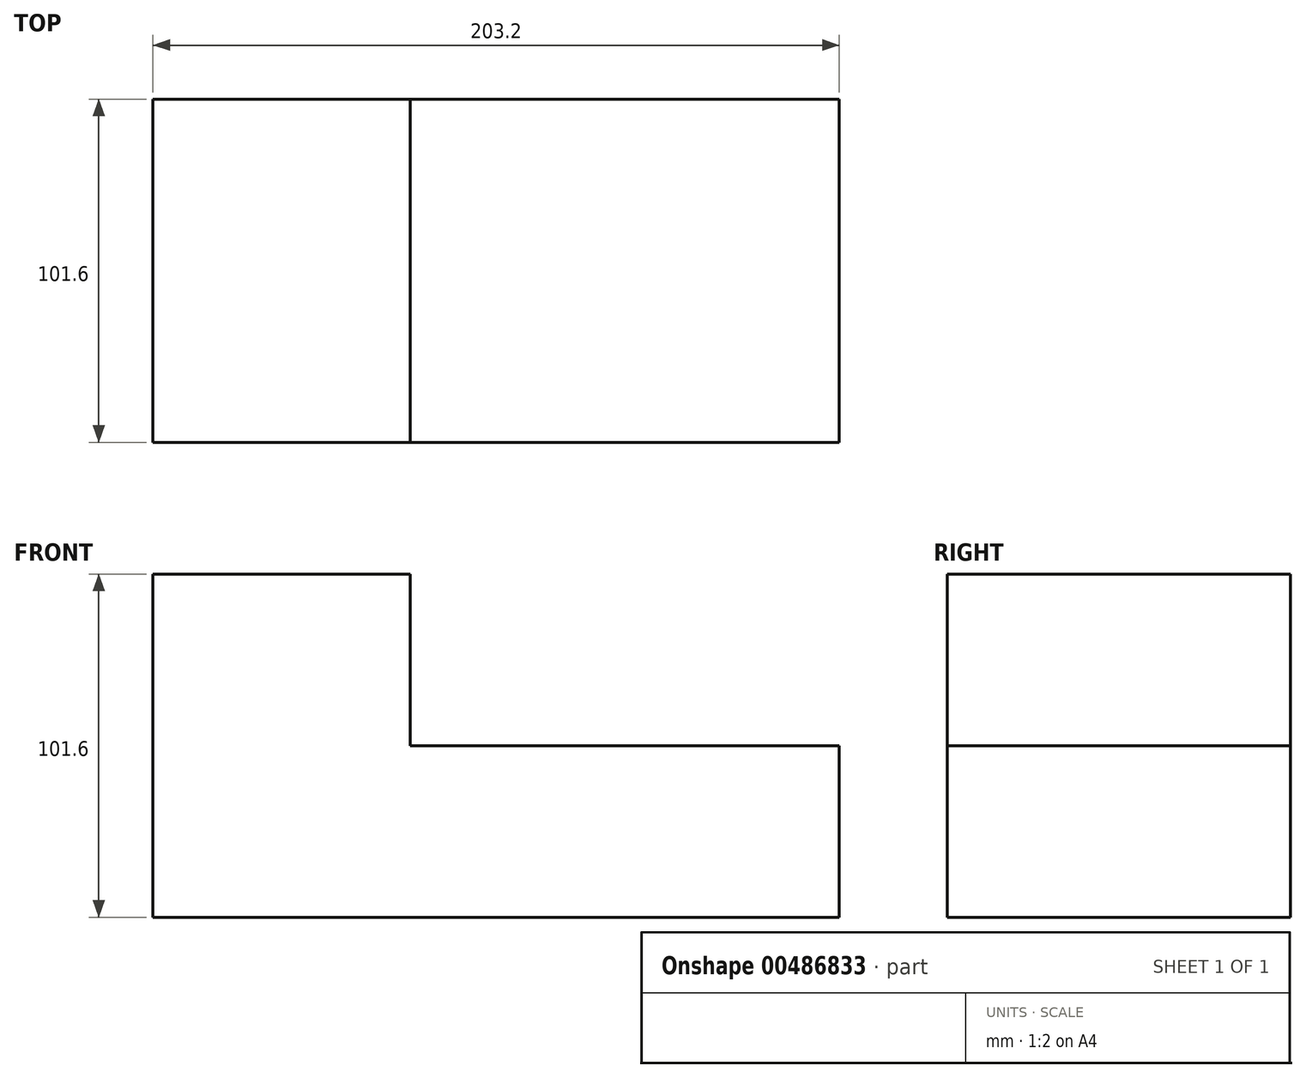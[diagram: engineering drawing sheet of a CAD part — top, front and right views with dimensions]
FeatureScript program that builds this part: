
annotation { "Feature Type Name" : "Feature", "Feature Type Description" : "" }
export const myFeature = defineFeature(function(context is Context, id is Id, definition is map)
    precondition{}
    {
        {
            var Q0;
            Q0=qCreatedBy(makeId("Front.planeOp"),FACE);
            var sketch = newSketch(context, id + "F0", { "sketchPlane" : qUnion([Q0])});
            skLineSegment(sketch, "E0.bottom", {"start": v(0, 0) * mm, "end": v(203.2, 0) * mm});
            skLineSegment(sketch, "E0.top", {"start": v(0, 50.8) * mm, "end": v(203.2, 50.8) * mm});
            skLineSegment(sketch, "E0.left", {"start": v(0, 0) * mm, "end": v(0, 50.8) * mm});
            skLineSegment(sketch, "E0.right", {"start": v(203.2, 0) * mm, "end": v(203.2, 50.8) * mm});
            skLineSegment(sketch, "E1.bottom", {"start": v(76.2, 50.8) * mm, "end": v(0, 50.8) * mm});
            skLineSegment(sketch, "E1.top", {"start": v(76.2, 101.6) * mm, "end": v(0, 101.6) * mm});
            skLineSegment(sketch, "E1.left", {"start": v(76.2, 50.8) * mm, "end": v(76.2, 101.6) * mm});
            skLineSegment(sketch, "E1.right", {"start": v(0, 50.8) * mm, "end": v(0, 101.6) * mm});
            skSolve(sketch);
        }
        {
            var Q0;
            Q0 = qSketchRegion(id + "F0", true);
            extrude(context, id + "F1", {"entities" : qUnion([Q0]), "depth" : 101.6 * mm});
        }
    });
